# Revit family: Basin-Wall-Caroma Care 700 Shelf RH1
name_source: partatom
category: Plumbing Fixtures
revit_build: Autodesk Revit 2014 (Build: 20131024_2115(x64)
units: mm (PartAtom-declared; Revit-internal decimal feet)

## types (1)
- Care 700 - 0 Tap Holes
    1 Taphole = No
    3 Tapholes = No
    Assembly Code = D2010310
    CW Connection = No
    Capacity_ANZRS = 9.3 L
    Default Elevation = 865 mm  [stored 2.83793 ft]
    Description = Caroma Care 700 RH Shelf Wall Basin
    HW Connection = No
    Height_ANZRS = 205 mm  [stored 0.672572 ft]
    Length_ANZRS = 700 mm  [stored 2.29659 ft]
    Manufacturer = GWA Bathrooms & Kitchens
    Material_ANZRS = Porcelain-White-Caroma
    Model = 873300W
    ModifiedIssue_ANZRS = 20141029.01 $
    Spout Penetration = 100 mm  [stored 0.328084 ft]
    Tap Penetrations = 100 mm  [stored 0.328084 ft]
    Type Comments = White Only, Overflow not available, Includes chrome plated brass waste
    URL = http://www.caroma.com.au
    Vent Connection = No
    WFU = 1
    Waste = Metal-Chrome-Caroma
    Waste Connection = Yes
    WasteOutlet_ANZRS = 0
    Width_ANZRS = 405 mm

note: [stored X ft] marks values corroborated as IEEE doubles in the binary element streams (Revit-internal decimal feet)

## geometry (parser evidence)
native form markers: Blend x12, Sweep x4
no freeform markers — native parametric forms only
